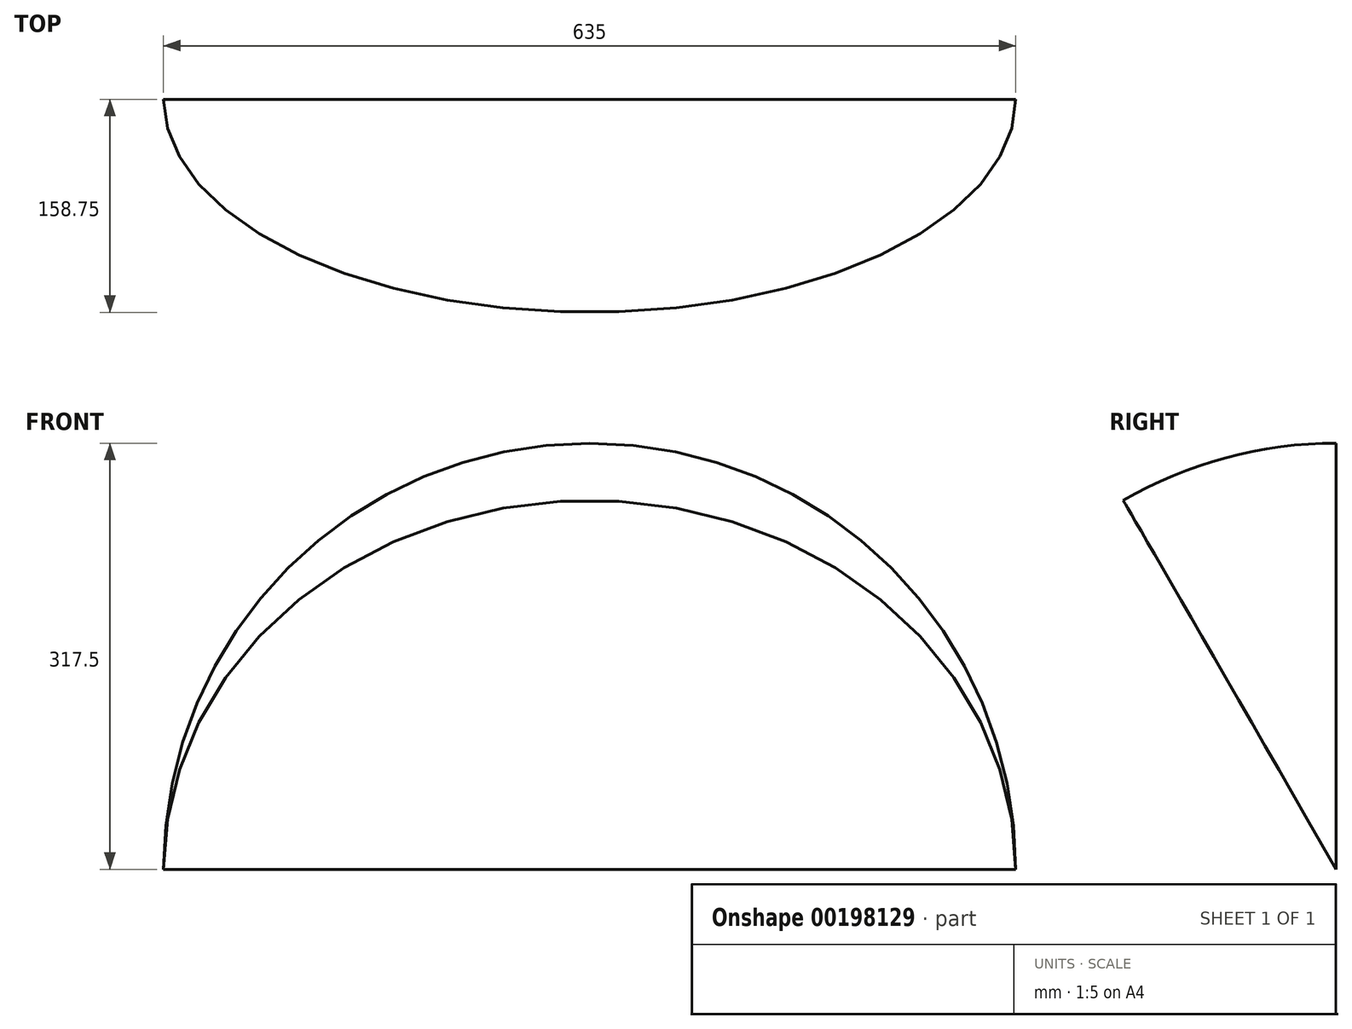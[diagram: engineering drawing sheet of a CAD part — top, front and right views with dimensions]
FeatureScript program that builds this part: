
annotation { "Feature Type Name" : "Feature", "Feature Type Description" : "" }
export const myFeature = defineFeature(function(context is Context, id is Id, definition is map)
    precondition{}
    {
        {
            var Q0;
            Q0=qCreatedBy(makeId("Front.planeOp"),FACE);
            var sketch = newSketch(context, id + "F0", { "sketchPlane" : qUnion([Q0])});
            skLineSegment(sketch, "E0", {"start": v(-681.05, 0) * mm, "end": v(566.25, 0) * mm});
            skCircle(sketch, "E1", {"center": v(0, 0) * mm, "radius": 317.5 * mm});
            skSolve(sketch);
        }
        {
            var Q0;
            {var subQ0=sQuery(id+"F0.wireOp",EDGE,"E1");var subQ1=sQuery(id+"F0.wireOp",EDGE,"E0");var subQ2=makeQuery(id+"F0.imprint","INTERSECT",VERTEX,{"disambiguationData":[OD(0.0)],"derivedFrom":[subQ1,subQ0]});Q0=makeQuery(id+"F0.imprint","IMPRINT",FACE,{"disambiguationData":[TD([[makeQuery(id+"F0.imprint","IMPRINT",EDGE,{"disambiguationData":[TD([[subQ2,-1.0]])],"derivedFrom":subQ1}),1.0]])]});}
            var Q1;
            Q1=sQuery(id+"F0.wireOp",EDGE,"E0");
            revolve(context, id + "F1", {"entities" : qUnion([Q0]), "axis" : qUnion([Q1]), "revolveType" : RevolveType.ONE_DIRECTION, "angle" : 30 * degree});
        }
    });
